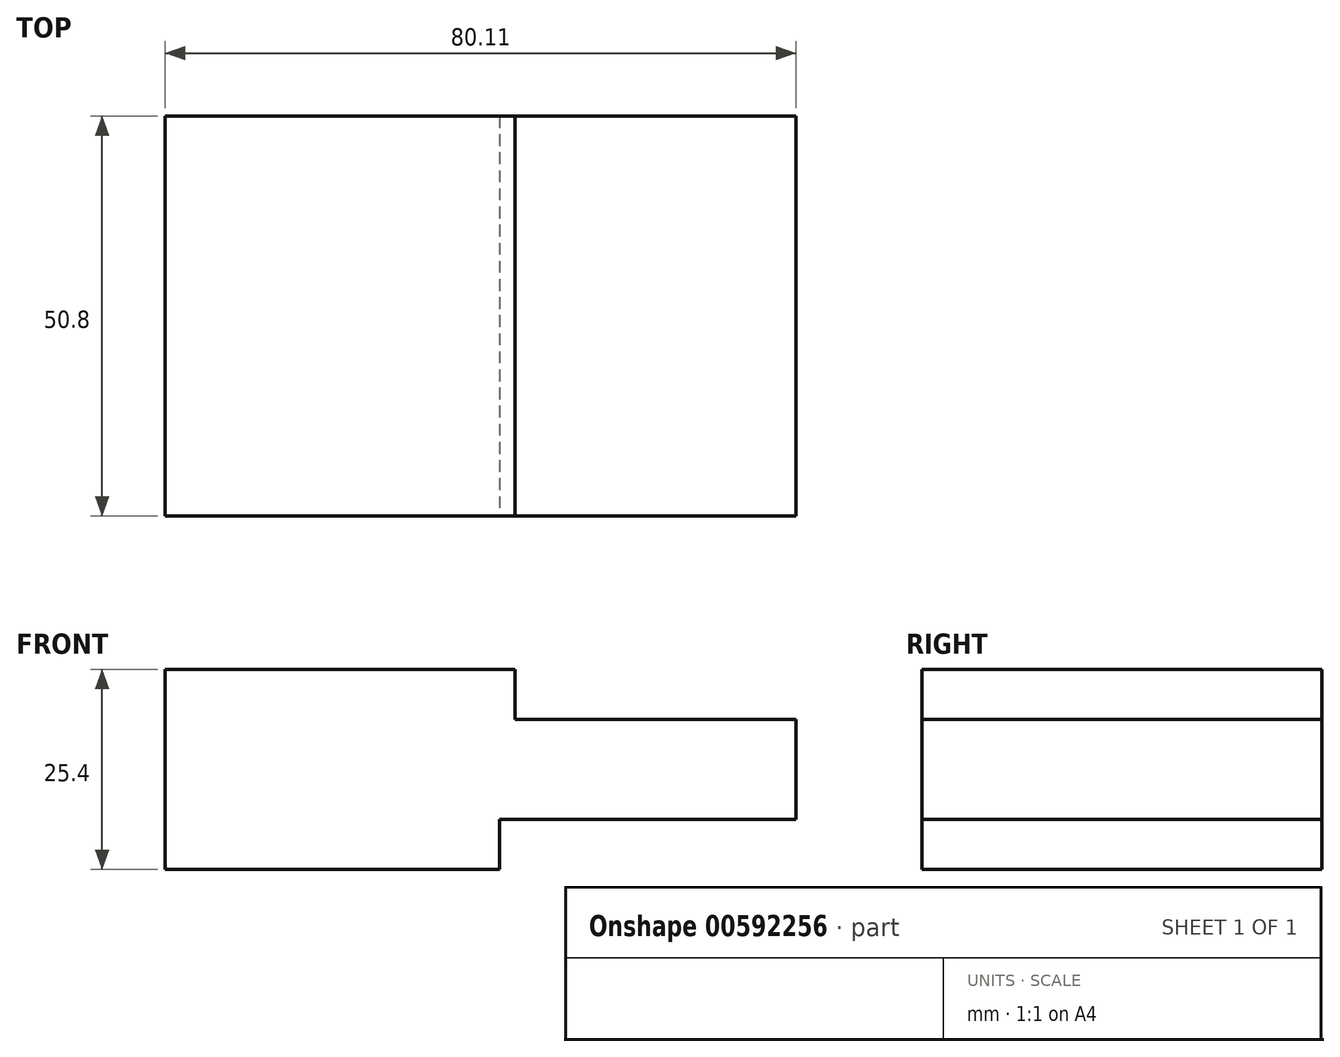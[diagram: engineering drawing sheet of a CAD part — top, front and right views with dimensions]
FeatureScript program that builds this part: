
annotation { "Feature Type Name" : "Feature", "Feature Type Description" : "" }
export const myFeature = defineFeature(function(context is Context, id is Id, definition is map)
    precondition{}
    {
        {
            var Q0;
            Q0=qCreatedBy(makeId("Front.planeOp"),FACE);
            var sketch = newSketch(context, id + "F0", { "sketchPlane" : qUnion([Q0])});
            skLineSegment(sketch, "E0", {"start": v(0, 0) * mm, "end": v(0, 25.4) * mm});
            skLineSegment(sketch, "E1", {"start": v(0, 25.4) * mm, "end": v(44.45, 25.4) * mm});
            skLineSegment(sketch, "E2", {"start": v(44.45, 25.4) * mm, "end": v(44.45, 19.05) * mm});
            skLineSegment(sketch, "E3", {"start": v(44.45, 19.05) * mm, "end": v(80.11, 19.05) * mm});
            skLineSegment(sketch, "E4", {"start": v(80.11, 19.05) * mm, "end": v(80.11, 6.35) * mm});
            skLineSegment(sketch, "E5", {"start": v(80.11, 6.35) * mm, "end": v(42.44, 6.35) * mm});
            skLineSegment(sketch, "E6", {"start": v(42.44, 6.35) * mm, "end": v(42.44, 0) * mm});
            skLineSegment(sketch, "E7", {"start": v(42.44, 0) * mm, "end": v(0, 0) * mm});
            skSolve(sketch);
        }
        {
            var Q0;
            Q0=makeQuery(id+"F0.imprint","IMPRINT",FACE,{"disambiguationData":[TD([[makeQuery(id+"F0.imprint","IMPRINT",EDGE,{"derivedFrom":sQuery(id+"F0.wireOp",EDGE,"E0")}),-1.0]])]});
            extrude(context, id + "F1", {"entities" : qUnion([Q0]), "oppositeDirection" : true, "depth" : 50.8 * mm, "offsetDistance" : 25.4 * mm});
        }
    });
